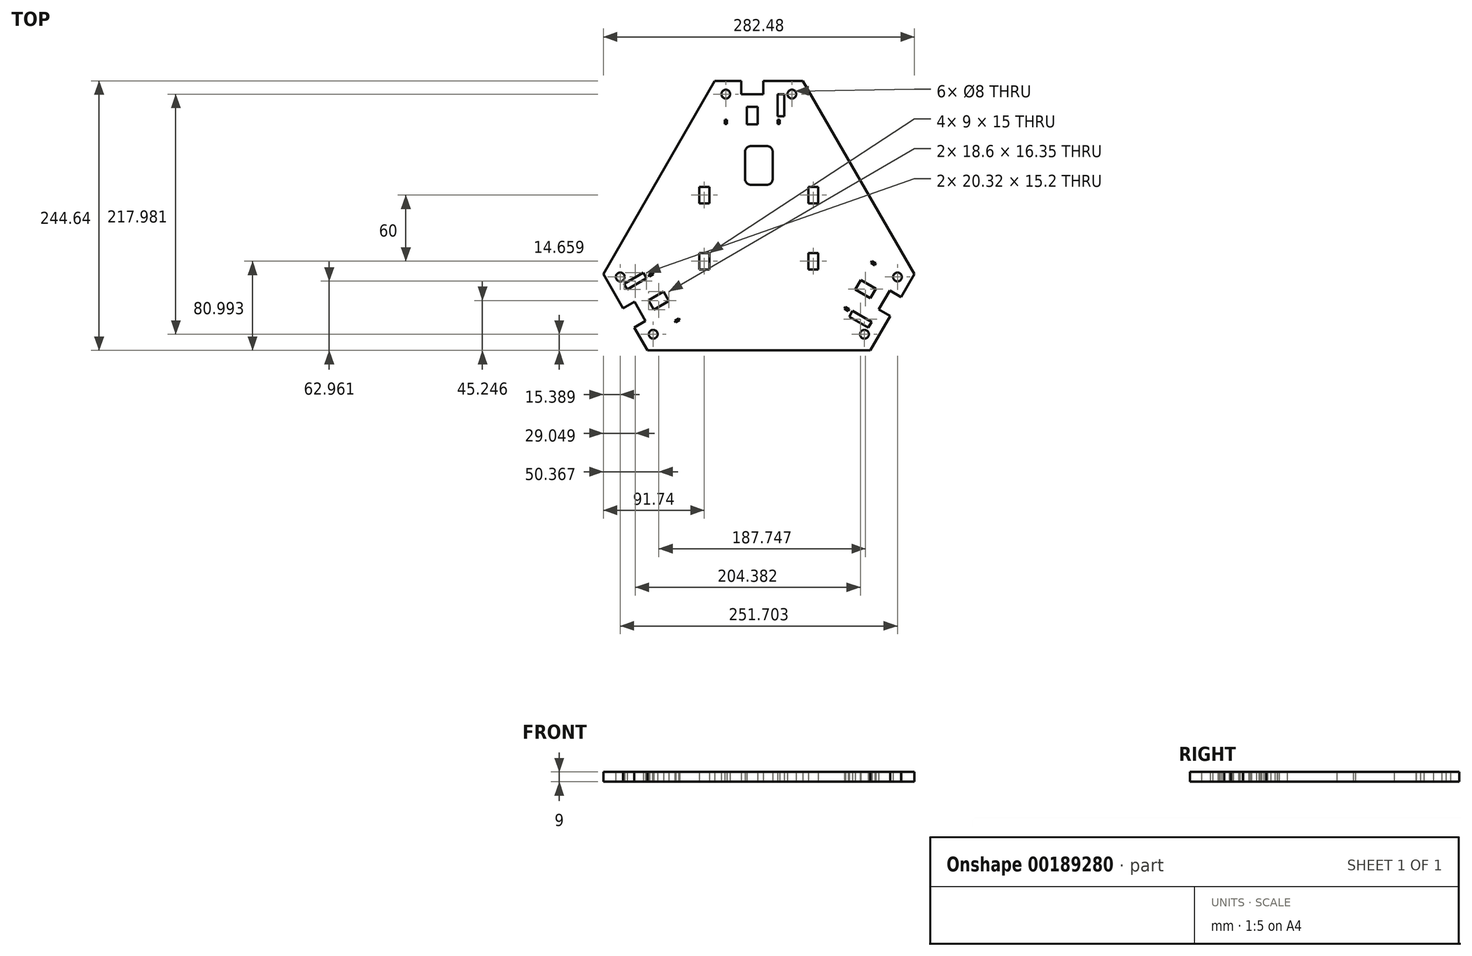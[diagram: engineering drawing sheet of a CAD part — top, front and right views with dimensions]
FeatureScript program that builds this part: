
annotation { "Feature Type Name" : "Feature", "Feature Type Description" : "" }
export const myFeature = defineFeature(function(context is Context, id is Id, definition is map)
    precondition{}
    {
        {
            var Q0;
            Q0=qCreatedBy(makeId("Top.planeOp"),FACE);
            var sketch = newSketch(context, id + "F0", { "sketchPlane" : qUnion([Q0])});
            skCircle(sketch, "E0.cCircle", {"center": v(0, 0) * mm, "radius": 140 * mm, "construction": true});
            skLineSegment(sketch, "E0.0", {"start": v(-40, 140) * mm, "end": v(40, 140) * mm});
            skLineSegment(sketch, "E0.1", {"start": v(40, 140) * mm, "end": v(141.24, -35.36) * mm});
            skLineSegment(sketch, "E0.2", {"start": v(141.24, -35.36) * mm, "end": v(101.24, -104.64) * mm});
            skLineSegment(sketch, "E0.3", {"start": v(101.24, -104.64) * mm, "end": v(-101.24, -104.64) * mm});
            skLineSegment(sketch, "E0.4", {"start": v(-101.24, -104.64) * mm, "end": v(-141.24, -35.36) * mm});
            skLineSegment(sketch, "E0.5", {"start": v(-141.24, -35.36) * mm, "end": v(-40, 140) * mm});
            skPoint(sketch, "E0.0.midPoint", {"position": v(0, 140) * mm});
            skLineSegment(sketch, "E1", {"start": v(0, 140) * mm, "end": v(0, 0) * mm, "construction": true});
            skCircle(sketch, "E2", {"center": v(-30, 128) * mm, "radius": 4 * mm});
            skCircle(sketch, "E3.MirrorC", {"center": v(30, 128) * mm, "radius": 4 * mm});
            skLineSegment(sketch, "E4", {"start": v(-16, 140) * mm, "end": v(-16, 128) * mm});
            skLineSegment(sketch, "E5", {"start": v(-16, 128) * mm, "end": v(4, 128) * mm});
            skLineSegment(sketch, "E6", {"start": v(4, 128) * mm, "end": v(4, 140) * mm});
            skLineSegment(sketch, "E7.bottom", {"start": v(17, 128) * mm, "end": v(23, 128) * mm});
            skLineSegment(sketch, "E7.top", {"start": v(17, 108) * mm, "end": v(23, 108) * mm});
            skLineSegment(sketch, "E7.left", {"start": v(17, 128) * mm, "end": v(17, 108) * mm});
            skLineSegment(sketch, "E7.right", {"start": v(23, 128) * mm, "end": v(23, 108) * mm});
            skLineSegment(sketch, "E8", {"start": v(-6, 140) * mm, "end": v(-6, 99.39) * mm, "construction": true});
            skLineSegment(sketch, "E9.bottom", {"start": v(15, 124.17) * mm, "end": v(-27, 124.17) * mm, "construction": true});
            skLineSegment(sketch, "E9.top", {"start": v(15, 89.17) * mm, "end": v(-27, 89.17) * mm, "construction": true});
            skLineSegment(sketch, "E9.left", {"start": v(15, 124.17) * mm, "end": v(15, 89.17) * mm, "construction": true});
            skLineSegment(sketch, "E9.right", {"start": v(-27, 124.17) * mm, "end": v(-27, 89.17) * mm, "construction": true});
            skPoint(sketch, "E9.middle", {"position": v(-6, 106.67) * mm});
            skLineSegment(sketch, "E10.bottom", {"start": v(17, 104.78) * mm, "end": v(19, 104.78) * mm});
            skLineSegment(sketch, "E10.top", {"start": v(17, 100.78) * mm, "end": v(19, 100.78) * mm});
            skLineSegment(sketch, "E10.left", {"start": v(17, 104.78) * mm, "end": v(17, 100.78) * mm});
            skLineSegment(sketch, "E10.right", {"start": v(19, 104.78) * mm, "end": v(19, 100.78) * mm});
            skLineSegment(sketch, "E11.MirrorCS", {"start": v(-29, 104.78) * mm, "end": v(-31, 104.78) * mm});
            skLineSegment(sketch, "E12.MirrorCS", {"start": v(-29, 100.78) * mm, "end": v(-31, 100.78) * mm});
            skLineSegment(sketch, "E13.MirrorCS", {"start": v(-31, 104.78) * mm, "end": v(-31, 100.78) * mm});
            skLineSegment(sketch, "E14.MirrorCS", {"start": v(-29, 104.78) * mm, "end": v(-29, 100.78) * mm});
            skLineSegment(sketch, "E15.bottom", {"start": v(-1.14, 100.46) * mm, "end": v(-10.86, 100.46) * mm});
            skLineSegment(sketch, "E15.top", {"start": v(-1.14, 116.33) * mm, "end": v(-10.86, 116.33) * mm});
            skLineSegment(sketch, "E15.left", {"start": v(-1.14, 100.46) * mm, "end": v(-1.14, 116.33) * mm});
            skLineSegment(sketch, "E15.right", {"start": v(-10.86, 100.46) * mm, "end": v(-10.86, 116.33) * mm});
            skPoint(sketch, "E15.middle", {"position": v(-6, 108.4) * mm});
            skLineSegment(sketch, "E16.1.0", {"start": v(-115.03, -49.1) * mm, "end": v(-84.72, -31.6) * mm, "construction": true});
            skLineSegment(sketch, "E16.1.1", {"start": v(-112.85, -60.54) * mm, "end": v(-123.24, -66.54) * mm});
            skLineSegment(sketch, "E16.1.2", {"start": v(-102.85, -77.86) * mm, "end": v(-112.85, -60.54) * mm});
            skLineSegment(sketch, "E16.1.3", {"start": v(-113.24, -83.86) * mm, "end": v(-102.85, -77.86) * mm});
            skCircle(sketch, "E16.1.4", {"center": v(-125.85, -38.02) * mm, "radius": 4 * mm});
            skCircle(sketch, "E16.1.5", {"center": v(-95.85, -89.98) * mm, "radius": 4 * mm});
            skLineSegment(sketch, "E16.1.6", {"start": v(-122.35, -44.08) * mm, "end": v(-105.03, -34.08) * mm});
            skLineSegment(sketch, "E16.1.7", {"start": v(-86.43, -51.22) * mm, "end": v(-100.17, -59.15) * mm});
            skPoint(sketch, "E16.1.8", {"position": v(-89.38, -58.53) * mm});
            skPoint(sketch, "E16.1.10", {"position": v(-121.24, -70) * mm});
            skLineSegment(sketch, "E16.1.11", {"start": v(-118.24, -75.2) * mm, "end": v(-83.07, -54.9) * mm, "construction": true});
            skLineSegment(sketch, "E16.1.12", {"start": v(-115.03, -49.1) * mm, "end": v(-94.03, -85.47) * mm, "construction": true});
            skLineSegment(sketch, "E16.1.13", {"start": v(-94.03, -85.47) * mm, "end": v(-63.72, -67.97) * mm, "construction": true});
            skLineSegment(sketch, "E16.1.14", {"start": v(-119.35, -49.28) * mm, "end": v(-102.03, -39.28) * mm});
            skLineSegment(sketch, "E16.1.15", {"start": v(-84.72, -31.6) * mm, "end": v(-63.72, -67.97) * mm, "construction": true});
            skPoint(sketch, "E16.1.16", {"position": v(-90.87, -59.4) * mm});
            skLineSegment(sketch, "E16.1.17", {"start": v(-100.17, -59.15) * mm, "end": v(-95.31, -67.57) * mm});
            skLineSegment(sketch, "E16.1.18", {"start": v(-81.57, -59.64) * mm, "end": v(-95.31, -67.57) * mm});
            skLineSegment(sketch, "E16.1.19", {"start": v(-86.43, -51.22) * mm, "end": v(-81.57, -59.64) * mm});
            skLineSegment(sketch, "E16.1.20", {"start": v(-72.78, -75.5) * mm, "end": v(-71.78, -77.24) * mm});
            skLineSegment(sketch, "E16.1.21", {"start": v(-76.24, -77.5) * mm, "end": v(-72.78, -75.5) * mm});
            skLineSegment(sketch, "E16.1.22", {"start": v(-75.24, -79.24) * mm, "end": v(-71.78, -77.24) * mm});
            skLineSegment(sketch, "E16.1.23", {"start": v(-119.35, -49.28) * mm, "end": v(-122.35, -44.08) * mm});
            skLineSegment(sketch, "E16.1.24", {"start": v(-76.24, -77.5) * mm, "end": v(-75.24, -79.24) * mm});
            skLineSegment(sketch, "E16.1.25", {"start": v(-100.24, -35.94) * mm, "end": v(-96.78, -33.94) * mm});
            skLineSegment(sketch, "E16.1.26", {"start": v(-99.24, -37.67) * mm, "end": v(-100.24, -35.94) * mm});
            skLineSegment(sketch, "E16.1.27", {"start": v(-99.24, -37.67) * mm, "end": v(-95.78, -35.67) * mm});
            skLineSegment(sketch, "E16.1.28", {"start": v(-102.03, -39.28) * mm, "end": v(-105.03, -34.08) * mm});
            skLineSegment(sketch, "E16.1.29", {"start": v(-95.78, -35.67) * mm, "end": v(-96.78, -33.94) * mm});
            skLineSegment(sketch, "E16.2.0", {"start": v(100.03, -75.07) * mm, "end": v(69.72, -57.57) * mm, "construction": true});
            skLineSegment(sketch, "E16.2.1", {"start": v(108.85, -67.46) * mm, "end": v(119.24, -73.46) * mm});
            skLineSegment(sketch, "E16.2.2", {"start": v(118.85, -50.14) * mm, "end": v(108.85, -67.46) * mm});
            skLineSegment(sketch, "E16.2.3", {"start": v(129.24, -56.14) * mm, "end": v(118.85, -50.14) * mm});
            skCircle(sketch, "E16.2.4", {"center": v(95.85, -89.98) * mm, "radius": 4 * mm});
            skCircle(sketch, "E16.2.5", {"center": v(125.85, -38.02) * mm, "radius": 4 * mm});
            skLineSegment(sketch, "E16.2.6", {"start": v(99.35, -83.92) * mm, "end": v(82.03, -73.92) * mm});
            skLineSegment(sketch, "E16.2.7", {"start": v(87.57, -49.24) * mm, "end": v(101.31, -57.18) * mm});
            skPoint(sketch, "E16.2.8", {"position": v(95.38, -48.14) * mm});
            skPoint(sketch, "E16.2.10", {"position": v(121.24, -70) * mm});
            skLineSegment(sketch, "E16.2.11", {"start": v(124.24, -64.8) * mm, "end": v(89.07, -44.5) * mm, "construction": true});
            skLineSegment(sketch, "E16.2.12", {"start": v(100.03, -75.07) * mm, "end": v(121.03, -38.7) * mm, "construction": true});
            skLineSegment(sketch, "E16.2.13", {"start": v(121.03, -38.7) * mm, "end": v(90.72, -21.2) * mm, "construction": true});
            skLineSegment(sketch, "E16.2.14", {"start": v(102.35, -78.72) * mm, "end": v(85.03, -68.72) * mm});
            skLineSegment(sketch, "E16.2.15", {"start": v(69.72, -57.57) * mm, "end": v(90.72, -21.2) * mm, "construction": true});
            skPoint(sketch, "E16.2.16", {"position": v(96.87, -49) * mm});
            skLineSegment(sketch, "E16.2.17", {"start": v(101.31, -57.18) * mm, "end": v(106.17, -48.76) * mm});
            skLineSegment(sketch, "E16.2.18", {"start": v(92.43, -40.83) * mm, "end": v(106.17, -48.76) * mm});
            skLineSegment(sketch, "E16.2.19", {"start": v(87.57, -49.24) * mm, "end": v(92.43, -40.83) * mm});
            skLineSegment(sketch, "E16.2.20", {"start": v(101.78, -25.28) * mm, "end": v(102.78, -23.54) * mm});
            skLineSegment(sketch, "E16.2.21", {"start": v(105.24, -27.28) * mm, "end": v(101.78, -25.28) * mm});
            skLineSegment(sketch, "E16.2.22", {"start": v(106.24, -25.54) * mm, "end": v(102.78, -23.54) * mm});
            skLineSegment(sketch, "E16.2.23", {"start": v(102.35, -78.72) * mm, "end": v(99.35, -83.92) * mm});
            skLineSegment(sketch, "E16.2.24", {"start": v(105.24, -27.28) * mm, "end": v(106.24, -25.54) * mm});
            skLineSegment(sketch, "E16.2.25", {"start": v(81.24, -68.84) * mm, "end": v(77.78, -66.84) * mm});
            skLineSegment(sketch, "E16.2.26", {"start": v(82.24, -67.11) * mm, "end": v(81.24, -68.84) * mm});
            skLineSegment(sketch, "E16.2.27", {"start": v(82.24, -67.11) * mm, "end": v(78.78, -65.11) * mm});
            skLineSegment(sketch, "E16.2.28", {"start": v(85.03, -68.72) * mm, "end": v(82.03, -73.92) * mm});
            skLineSegment(sketch, "E16.2.29", {"start": v(78.78, -65.11) * mm, "end": v(77.78, -66.84) * mm});
            skLineSegment(sketch, "E17.bottom", {"start": v(7.5, 80.75) * mm, "end": v(-7.5, 80.75) * mm});
            skLineSegment(sketch, "E17.top", {"start": v(7.5, 45.75) * mm, "end": v(-7.5, 45.75) * mm});
            skLineSegment(sketch, "E17.left", {"start": v(12.5, 75.75) * mm, "end": v(12.5, 50.75) * mm});
            skLineSegment(sketch, "E17.right", {"start": v(-12.5, 75.75) * mm, "end": v(-12.5, 50.75) * mm});
            skPoint(sketch, "E17.middle", {"position": v(0, 63.25) * mm});
            skPoint(sketch, "E18.visualSharp", {"position": v(-12.5, 80.75) * mm});
            skArc(sketch, "E18.filletArc", {"start": v(-7.5, 80.75) * mm, "mid": v(-11.04, 79.29) * mm, "end": v(-12.5, 75.75) * mm});
            skPoint(sketch, "E19.visualSharp", {"position": v(12.5, 80.75) * mm});
            skArc(sketch, "E19.filletArc", {"start": v(12.5, 75.75) * mm, "mid": v(11.04, 79.29) * mm, "end": v(7.5, 80.75) * mm});
            skPoint(sketch, "E20.visualSharp", {"position": v(-12.5, 45.75) * mm});
            skArc(sketch, "E20.filletArc", {"start": v(-12.5, 50.75) * mm, "mid": v(-11.04, 47.21) * mm, "end": v(-7.5, 45.75) * mm});
            skPoint(sketch, "E21.visualSharp", {"position": v(12.5, 45.75) * mm});
            skArc(sketch, "E21.filletArc", {"start": v(7.5, 45.75) * mm, "mid": v(11.04, 47.21) * mm, "end": v(12.5, 50.75) * mm});
            skLineSegment(sketch, "E22.bottom", {"start": v(-45, 43.85) * mm, "end": v(-54, 43.85) * mm});
            skLineSegment(sketch, "E22.top", {"start": v(-45, 28.85) * mm, "end": v(-54, 28.85) * mm});
            skLineSegment(sketch, "E22.left", {"start": v(-45, 43.85) * mm, "end": v(-45, 28.85) * mm});
            skLineSegment(sketch, "E22.right", {"start": v(-54, 43.85) * mm, "end": v(-54, 28.85) * mm});
            skPoint(sketch, "E22.middle", {"position": v(-49.5, 36.35) * mm});
            skPoint(sketch, "E23", {"position": v(17, 118) * mm});
            skLineSegment(sketch, "E24.MirrorCS", {"start": v(45, 43.85) * mm, "end": v(45, 28.85) * mm});
            skLineSegment(sketch, "E25.MirrorCS", {"start": v(54, 43.85) * mm, "end": v(54, 28.85) * mm});
            skPoint(sketch, "E26.MirrorP", {"position": v(49.5, 36.35) * mm});
            skLineSegment(sketch, "E27.MirrorCS", {"start": v(45, 43.85) * mm, "end": v(54, 43.85) * mm});
            skLineSegment(sketch, "E28.MirrorCS", {"start": v(45, 28.85) * mm, "end": v(54, 28.85) * mm});
            skLineSegment(sketch, "E29.0.1.0", {"start": v(-54, -16.15) * mm, "end": v(-54, -31.15) * mm});
            skPoint(sketch, "E29.0.1.1", {"position": v(-49.5, -23.65) * mm});
            skLineSegment(sketch, "E29.0.1.2", {"start": v(-45, -16.15) * mm, "end": v(-54, -16.15) * mm});
            skLineSegment(sketch, "E29.0.1.3", {"start": v(-45, -31.15) * mm, "end": v(-54, -31.15) * mm});
            skLineSegment(sketch, "E29.0.1.4", {"start": v(-45, -16.15) * mm, "end": v(-45, -31.15) * mm});
            skPoint(sketch, "E29.0.1.5", {"position": v(49.5, -23.65) * mm});
            skLineSegment(sketch, "E29.0.1.6", {"start": v(45, -16.15) * mm, "end": v(45, -31.15) * mm});
            skLineSegment(sketch, "E29.0.1.7", {"start": v(54, -16.15) * mm, "end": v(54, -31.15) * mm});
            skLineSegment(sketch, "E29.0.1.8", {"start": v(45, -16.15) * mm, "end": v(54, -16.15) * mm});
            skLineSegment(sketch, "E29.0.1.9", {"start": v(45, -31.15) * mm, "end": v(54, -31.15) * mm});
            skLineSegment(sketch, "E29.direction1", {"start": v(-54, 28.85) * mm, "end": v(-29, 28.85) * mm, "construction": true});
            skLineSegment(sketch, "E29.direction2", {"start": v(-54, 28.85) * mm, "end": v(-54, -31.15) * mm, "construction": true});
            skSolve(sketch);
        }
        {
            var Q0;
            {var subQ8=sQuery(id+"F0.wireOp",EDGE,"E0.1");Q0=makeQuery(id+"F0.imprint","IMPRINT",FACE,{"disambiguationData":[TD([[makeQuery(id+"F0.imprint","IMPRINT",EDGE,{"derivedFrom":subQ8}),-1.0]])]});}
            extrude(context, id + "F1", {"entities" : qUnion([Q0]), "depth" : 9 * mm});
        }
    });
